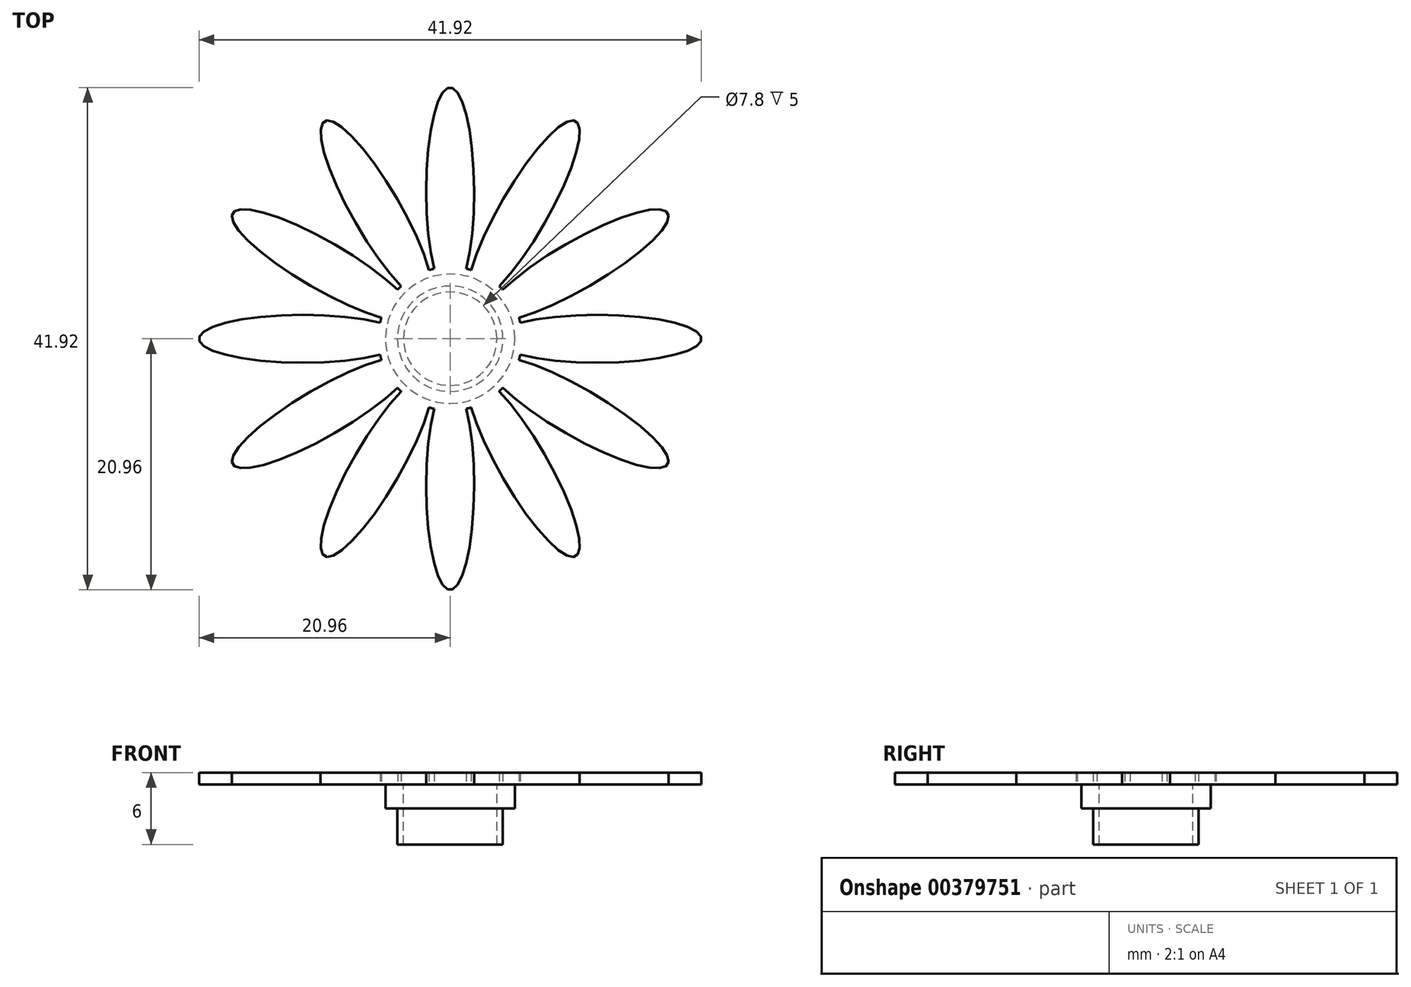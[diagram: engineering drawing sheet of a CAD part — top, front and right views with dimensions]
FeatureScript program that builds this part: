
annotation { "Feature Type Name" : "Feature", "Feature Type Description" : "" }
export const myFeature = defineFeature(function(context is Context, id is Id, definition is map)
    precondition{}
    {
        {
            var Q0;
            Q0=qCreatedBy(makeId("Top.planeOp"),FACE);
            var sketch = newSketch(context, id + "F0", { "sketchPlane" : qUnion([Q0])});
            skCircle(sketch, "E0", {"center": v(0, 0) * mm, "radius": 6 * mm});
            skEllipse(sketch, "E1", {"center": v(0, 12.28) * mm, "majorRadius": 8.68 * mm, "minorRadius": 2 * mm, "majorAxis": v(0, -1)});
            skSolve(sketch);
        }
        {
            var Q0;
            {var subQ0=sQuery(id+"F0.wireOp",EDGE,"E1");var subQ1=sQuery(id+"F0.wireOp",EDGE,"E0");var subQ2=makeQuery(id+"F0.imprint","INTERSECT",VERTEX,{"disambiguationData":[OD(0.0)],"derivedFrom":[subQ1,subQ0]});Q0=makeQuery(id+"F0.imprint","IMPRINT",FACE,{"disambiguationData":[TD([[makeQuery(id+"F0.imprint","IMPRINT",EDGE,{"disambiguationData":[TD([[subQ2,-1.0]])],"derivedFrom":subQ1}),1.0]])]});}
            var Q1;
            {var subQ0=sQuery(id+"F0.wireOp",EDGE,"E1");var subQ1=sQuery(id+"F0.wireOp",EDGE,"E0");var subQ2=makeQuery(id+"F0.imprint","INTERSECT",VERTEX,{"disambiguationData":[OD(0.0)],"derivedFrom":[subQ1,subQ0]});Q1=makeQuery(id+"F0.imprint","IMPRINT",FACE,{"disambiguationData":[TD([[makeQuery(id+"F0.imprint","IMPRINT",EDGE,{"disambiguationData":[TD([[subQ2,1.0]])],"derivedFrom":subQ1}),-1.0]])]});}
            var Q2;
            {var subQ0=sQuery(id+"F0.wireOp",EDGE,"E1");var subQ1=sQuery(id+"F0.wireOp",EDGE,"E0");var subQ2=makeQuery(id+"F0.imprint","INTERSECT",VERTEX,{"disambiguationData":[OD(0.0)],"derivedFrom":[subQ1,subQ0]});Q2=makeQuery(id+"F0.imprint","IMPRINT",FACE,{"disambiguationData":[TD([[makeQuery(id+"F0.imprint","IMPRINT",EDGE,{"disambiguationData":[TD([[subQ2,1.0]])],"derivedFrom":subQ1}),1.0]])]});}
            extrude(context, id + "F1", {"entities" : qUnion([Q0, Q1, Q2]), "depth" : 1 * mm, "offsetDistance" : 25 * mm});
        }
        {
            var Q0;
            Q0=qCreatedBy(makeId("Front.planeOp"),FACE);
            var sketch = newSketch(context, id + "F2", { "sketchPlane" : qUnion([Q0])});
            skLineSegment(sketch, "E2", {"start": v(0, 17.6) * mm, "end": v(0, 0) * mm, "construction": true});
            skSolve(sketch);
        }
        {
            var Q0;
            Q0=makeQuery(id+"F1.opExtrude","SWEPT_BODY",BODY,{"disambiguationData":[OSD([sQuery(id+"F0.wireOp",EDGE,"E0"),sQuery(id+"F0.wireOp",EDGE,"E1")])]});
            var Q1;
            Q1=sQuery(id+"F2.wireOp",EDGE,"E2");
            circularPattern(context, id + "F3", {"entities" : qUnion([Q0]), "axis" : qUnion([Q1]), "angle" : 360 * degree, "instanceCount" : 12, "equalSpace" : true, "computeTransformsWithoutBuiltin" : true});
        }
        {
            var Q0;
            Q0=qCreatedBy(makeId("Top.planeOp"),FACE);
            var sketch = newSketch(context, id + "F4", { "sketchPlane" : qUnion([Q0])});
            skCircle(sketch, "E3", {"center": v(0, 0) * mm, "radius": 4.4 * mm});
            skCircle(sketch, "E4", {"center": v(0, 0) * mm, "radius": 3.9 * mm});
            skCircle(sketch, "E5", {"center": v(0, 0) * mm, "radius": 5.4 * mm});
            skSolve(sketch);
        }
        {
            var Q0;
            Q0=makeQuery(id+"F4.imprint","IMPRINT",FACE,{"disambiguationData":[TD([[makeQuery(id+"F4.imprint","IMPRINT",EDGE,{"derivedFrom":sQuery(id+"F4.wireOp",EDGE,"E3")}),1.0]])]});
            extrude(context, id + "F5", {"entities" : qUnion([Q0]), "operationType" : NewBodyOperationType.ADD, "oppositeDirection" : true, "depth" : 5 * mm, "offsetDistance" : 25 * mm});
        }
        {
            var Q0;
            Q0=makeQuery(id+"F4.imprint","IMPRINT",FACE,{"disambiguationData":[TD([[makeQuery(id+"F4.imprint","IMPRINT",EDGE,{"derivedFrom":sQuery(id+"F4.wireOp",EDGE,"E3")}),-1.0]])]});
            extrude(context, id + "F6", {"entities" : qUnion([Q0]), "operationType" : NewBodyOperationType.ADD, "oppositeDirection" : true, "depth" : 2 * mm, "offsetDistance" : 25 * mm});
        }
    });
